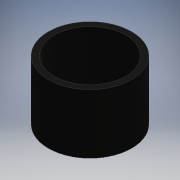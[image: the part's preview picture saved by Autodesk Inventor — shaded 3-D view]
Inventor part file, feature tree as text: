
AUTODESK INVENTOR PART (.ipt)
format: ipt  version: 2016 (Build 200138000, 138)  size: 91,136 bytes
history: native  units: mm
features: other x1, extrude x1, sketch x1
ambient origin geometry x8: Origin, YZ Plane, XZ Plane, XY Plane, X Axis, Y Axis, Z Axis, Center Point
bodies: Body1 (feature_tree)
feature tree (3):
  other  "ソリッド1"
  extrude  "押し出し1"  Depth=14.0mm
  sketch  "スケッチ1"
